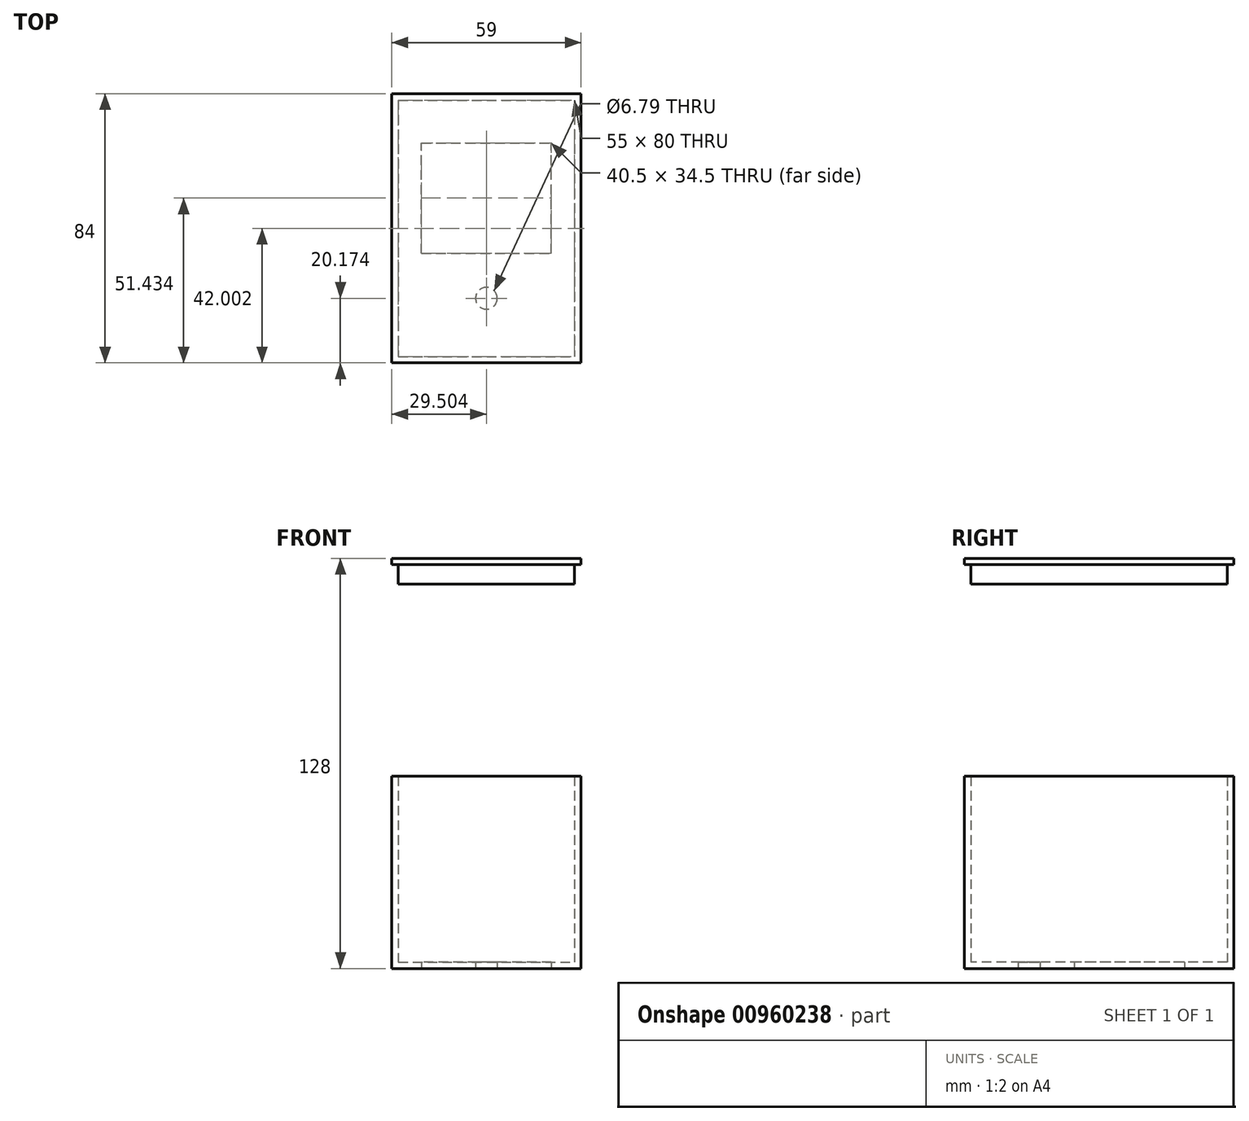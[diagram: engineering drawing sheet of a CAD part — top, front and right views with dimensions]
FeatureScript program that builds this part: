
annotation { "Feature Type Name" : "Feature", "Feature Type Description" : "" }
export const myFeature = defineFeature(function(context is Context, id is Id, definition is map)
    precondition{}
    {
        {
            var Q0;
            Q0=qCreatedBy(makeId("Top.planeOp"),FACE);
            var sketch = newSketch(context, id + "F0", { "sketchPlane" : qUnion([Q0])});
            skLineSegment(sketch, "E0.bottom", {"start": v(-28.16, 46.32) * mm, "end": v(26.84, 46.32) * mm});
            skLineSegment(sketch, "E0.top", {"start": v(-28.16, -33.68) * mm, "end": v(26.84, -33.68) * mm});
            skLineSegment(sketch, "E0.left", {"start": v(-28.16, 46.32) * mm, "end": v(-28.16, -33.68) * mm});
            skLineSegment(sketch, "E0.right", {"start": v(26.84, 46.32) * mm, "end": v(26.84, -33.68) * mm});
            skLineSegment(sketch, "E1.0", {"start": v(-30.16, 48.32) * mm, "end": v(28.84, 48.32) * mm});
            skLineSegment(sketch, "E1.1", {"start": v(-30.16, 48.32) * mm, "end": v(-30.16, -35.68) * mm});
            skLineSegment(sketch, "E1.2", {"start": v(-30.16, -35.68) * mm, "end": v(28.84, -35.68) * mm});
            skLineSegment(sketch, "E1.3", {"start": v(28.84, 48.32) * mm, "end": v(28.84, -35.68) * mm});
            skLineSegment(sketch, "E2", {"start": v(-0.66, -33.68) * mm, "end": v(-0.66, 46.32) * mm, "construction": true});
            skPoint(sketch, "E3", {"position": v(-0.66, -3.36) * mm});
            skSolve(sketch);
        }
        {
            var Q0;
            Q0=makeQuery(id+"F0.imprint","IMPRINT",FACE,{"disambiguationData":[TD([[makeQuery(id+"F0.imprint","IMPRINT",EDGE,{"derivedFrom":sQuery(id+"F0.wireOp",EDGE,"E0.bottom")}),-1.0]])]});
            extrude(context, id + "F1", {"entities" : qUnion([Q0]), "depth" : 2 * mm, "offsetDistance" : 25 * mm});
        }
        {
            var Q0;
            Q0=makeQuery(id+"F0.imprint","IMPRINT",FACE,{"disambiguationData":[TD([[makeQuery(id+"F0.imprint","IMPRINT",EDGE,{"derivedFrom":sQuery(id+"F0.wireOp",EDGE,"E0.bottom")}),1.0]])]});
            extrude(context, id + "F2", {"entities" : qUnion([Q0]), "operationType" : NewBodyOperationType.ADD, "depth" : 60 * mm, "offsetDistance" : 25 * mm});
        }
        {
            var Q0;
            Q0=makeQuery(id+"F1.opExtrude","CAP_FACE",FACE,{"disambiguationData":[OSD([sQuery(id+"F0.wireOp",EDGE,"E0.bottom"),sQuery(id+"F0.wireOp",EDGE,"E0.top"),sQuery(id+"F0.wireOp",EDGE,"E0.left"),sQuery(id+"F0.wireOp",EDGE,"E0.right")])],"isStart":false});
            var Q1;
            Q1=makeQuery(id+"F0.imprint","IMPRINT",FACE,{"disambiguationData":[TD([[makeQuery(id+"F0.imprint","IMPRINT",EDGE,{"derivedFrom":sQuery(id+"F0.wireOp",EDGE,"E0.bottom")}),-1.0]])]});
            var Q2;
            Q2=makeQuery(id+"F0.imprint","IMPRINT",FACE,{"disambiguationData":[TD([[makeQuery(id+"F0.imprint","IMPRINT",EDGE,{"derivedFrom":sQuery(id+"F0.wireOp",EDGE,"twfDnLaG-Envw-JZLl-0pYV-BHphajt3gSDh.bottom")}),1.0]])]});
            extrude(context, id + "F3", {"entities" : qUnion([Q0, Q1, Q2]), "depth" : 126 * mm, "offsetDistance" : 25 * mm, "hasSecondDirection" : true, "secondDirectionOppositeDirection" : false, "secondDirectionDepth" : 120 * mm});
        }
        {
            var Q0;
            Q0=makeQuery(id+"F0.imprint","IMPRINT",FACE,{"disambiguationData":[TD([[makeQuery(id+"F0.imprint","IMPRINT",EDGE,{"derivedFrom":sQuery(id+"F0.wireOp",EDGE,"E0.bottom")}),1.0]])]});
            var Q1;
            Q1=makeQuery(id+"F0.imprint","IMPRINT",FACE,{"disambiguationData":[TD([[makeQuery(id+"F0.imprint","IMPRINT",EDGE,{"derivedFrom":sQuery(id+"F0.wireOp",EDGE,"twfDnLaG-Envw-JZLl-0pYV-BHphajt3gSDh.bottom")}),1.0]])]});
            extrude(context, id + "F4", {"entities" : qUnion([Q0, Q1]), "operationType" : NewBodyOperationType.ADD, "depth" : (128) * mm, "offsetDistance" : 25 * mm, "hasSecondDirection" : true, "secondDirectionOppositeDirection" : false, "secondDirectionDepth" : 126 * mm});
        }
        {
            var Q0;
            Q0=makeQuery(id+"F0.imprint","IMPRINT",FACE,{"disambiguationData":[TD([[makeQuery(id+"F0.imprint","IMPRINT",EDGE,{"derivedFrom":sQuery(id+"F0.wireOp",EDGE,"E0.bottom")}),-1.0]])]});
            var sketch = newSketch(context, id + "F5", { "sketchPlane" : qUnion([Q0])});
            skCircle(sketch, "E4", {"center": v(-0.66, -15.5) * mm, "radius": 3.4 * mm});
            skLineSegment(sketch, "E5.bottom", {"start": v(-20.9, -1.5) * mm, "end": v(19.6, -1.5) * mm});
            skLineSegment(sketch, "E5.top", {"start": v(-20.9, 33) * mm, "end": v(19.6, 33) * mm});
            skLineSegment(sketch, "E5.left", {"start": v(-20.9, -1.5) * mm, "end": v(-20.9, 33) * mm});
            skLineSegment(sketch, "E5.right", {"start": v(19.6, -1.5) * mm, "end": v(19.6, 33) * mm});
            skPoint(sketch, "E6", {"position": v(-0.66, 33) * mm});
            skSolve(sketch);
        }
        {
            var Q0;
            Q0=makeQuery(id+"F5.imprint","IMPRINT",FACE,{"disambiguationData":[TD([[makeQuery(id+"F5.imprint","IMPRINT",EDGE,{"derivedFrom":sQuery(id+"F5.wireOp",EDGE,"E4")}),1.0]])]});
            var Q1;
            Q1=makeQuery(id+"F5.imprint","IMPRINT",FACE,{"disambiguationData":[TD([[makeQuery(id+"F5.imprint","IMPRINT",EDGE,{"derivedFrom":sQuery(id+"F5.wireOp",EDGE,"E5.bottom")}),1.0]])]});
            extrude(context, id + "F6", {"entities" : qUnion([Q0, Q1]), "operationType" : NewBodyOperationType.REMOVE, "depth" : 16.7 * mm, "offsetDistance" : 25 * mm});
        }
    });
